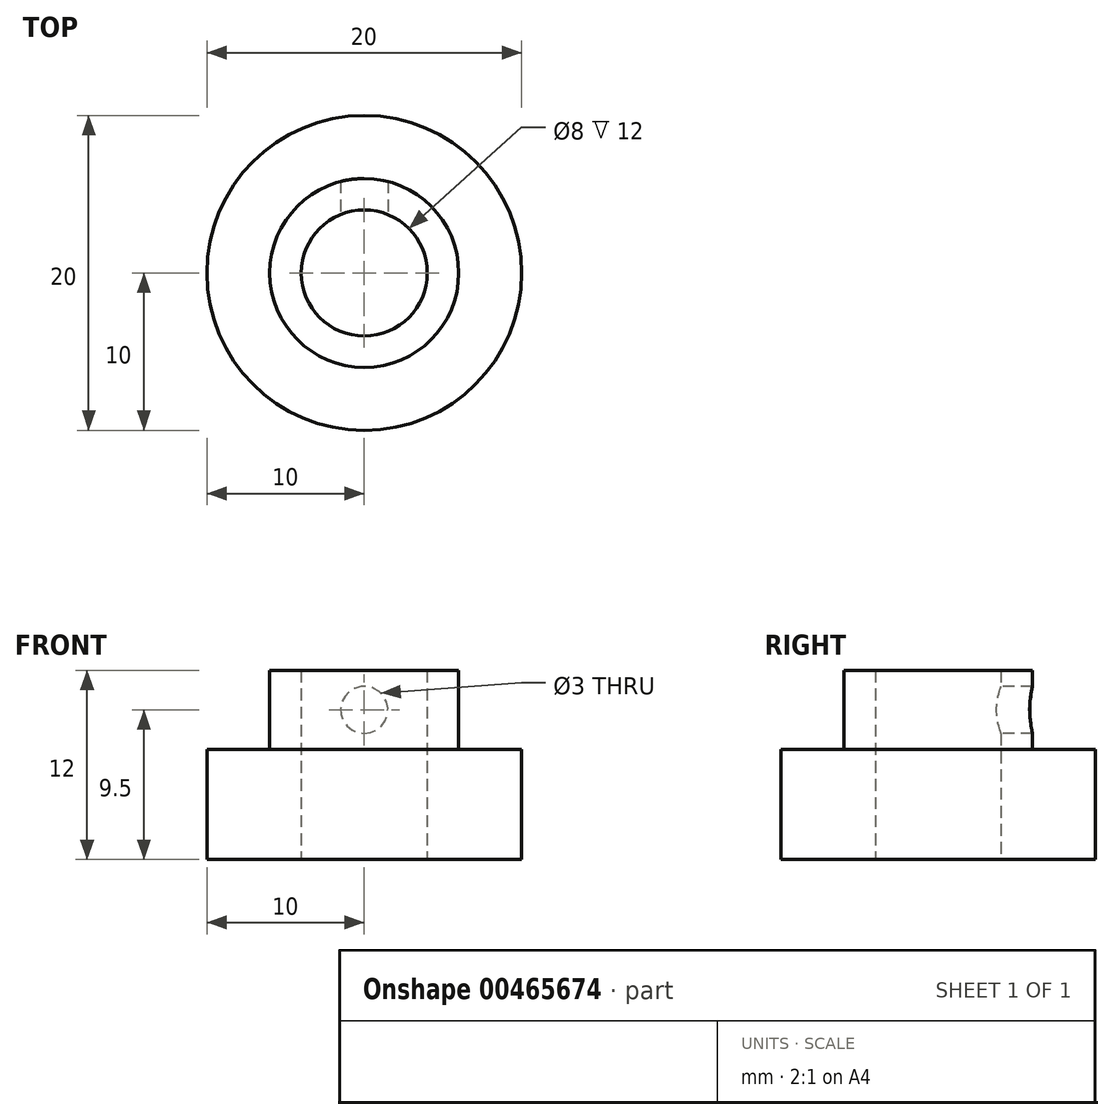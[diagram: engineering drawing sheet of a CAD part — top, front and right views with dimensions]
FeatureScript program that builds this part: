
annotation { "Feature Type Name" : "Feature", "Feature Type Description" : "" }
export const myFeature = defineFeature(function(context is Context, id is Id, definition is map)
    precondition{}
    {
        {
            var Q0;
            Q0=qCreatedBy(makeId("Front.planeOp"),FACE);
            var sketch = newSketch(context, id + "F0", { "sketchPlane" : qUnion([Q0])});
            skLineSegment(sketch, "E0", {"start": v(-10, 0) * mm, "end": v(-10, 7) * mm});
            skLineSegment(sketch, "E1", {"start": v(-10, 7) * mm, "end": v(-6, 7) * mm});
            skLineSegment(sketch, "E2", {"start": v(-6, 7) * mm, "end": v(-6, 12) * mm});
            skLineSegment(sketch, "E3", {"start": v(-6, 12) * mm, "end": v(-4, 12) * mm});
            skLineSegment(sketch, "E4", {"start": v(-4, 12) * mm, "end": v(-4, 0) * mm});
            skLineSegment(sketch, "E5", {"start": v(-4, 0) * mm, "end": v(-10, 0) * mm});
            skLineSegment(sketch, "E6", {"start": v(0, 0) * mm, "end": v(0, 15.5) * mm, "construction": true});
            skSolve(sketch);
        }
        {
            var Q0;
            Q0=makeQuery(id+"F0.imprint","IMPRINT",FACE,{"disambiguationData":[TD([[makeQuery(id+"F0.imprint","IMPRINT",EDGE,{"derivedFrom":sQuery(id+"F0.wireOp",EDGE,"E0")}),-1.0]])]});
            var Q1;
            Q1=sQuery(id+"F0.wireOp",EDGE,"E6");
            revolve(context, id + "F1", {"entities" : qUnion([Q0]), "axis" : qUnion([Q1]), "revolveType" : RevolveType.FULL});
        }
        {
            var Q0;
            Q0=qCreatedBy(makeId("Front.planeOp"),FACE);
            var sketch = newSketch(context, id + "F2", { "sketchPlane" : qUnion([Q0])});
            skCircle(sketch, "E7", {"center": v(0, 9.5) * mm, "radius": 1.5 * mm});
            skLineSegment(sketch, "E8", {"start": v(0, 9.5) * mm, "end": v(0, 12) * mm, "construction": true});
            skLineSegment(sketch, "E9", {"start": v(0, 9.5) * mm, "end": v(0, 7) * mm, "construction": true});
            skSolve(sketch);
        }
        {
            var Q0;
            Q0=makeQuery(id+"F2.imprint","IMPRINT",FACE,{"disambiguationData":[TD([[makeQuery(id+"F2.imprint","IMPRINT",EDGE,{"derivedFrom":sQuery(id+"F2.wireOp",EDGE,"E7")}),1.0]])]});
            var Q1;
            Q1=makeQuery(id+"F1.opRevolve","SWEPT_FACE",FACE,{"disambiguationData":[OSD([sQuery(id+"F0.wireOp",EDGE,"E2")])]});
            extrude(context, id + "F3", {"entities" : qUnion([Q0]), "operationType" : NewBodyOperationType.REMOVE, "endBound" : BoundingType.UP_TO_SURFACE, "oppositeDirection" : true, "endBoundEntityFace" : qUnion([Q1]), "depth" : 20 * mm});
        }
    });
